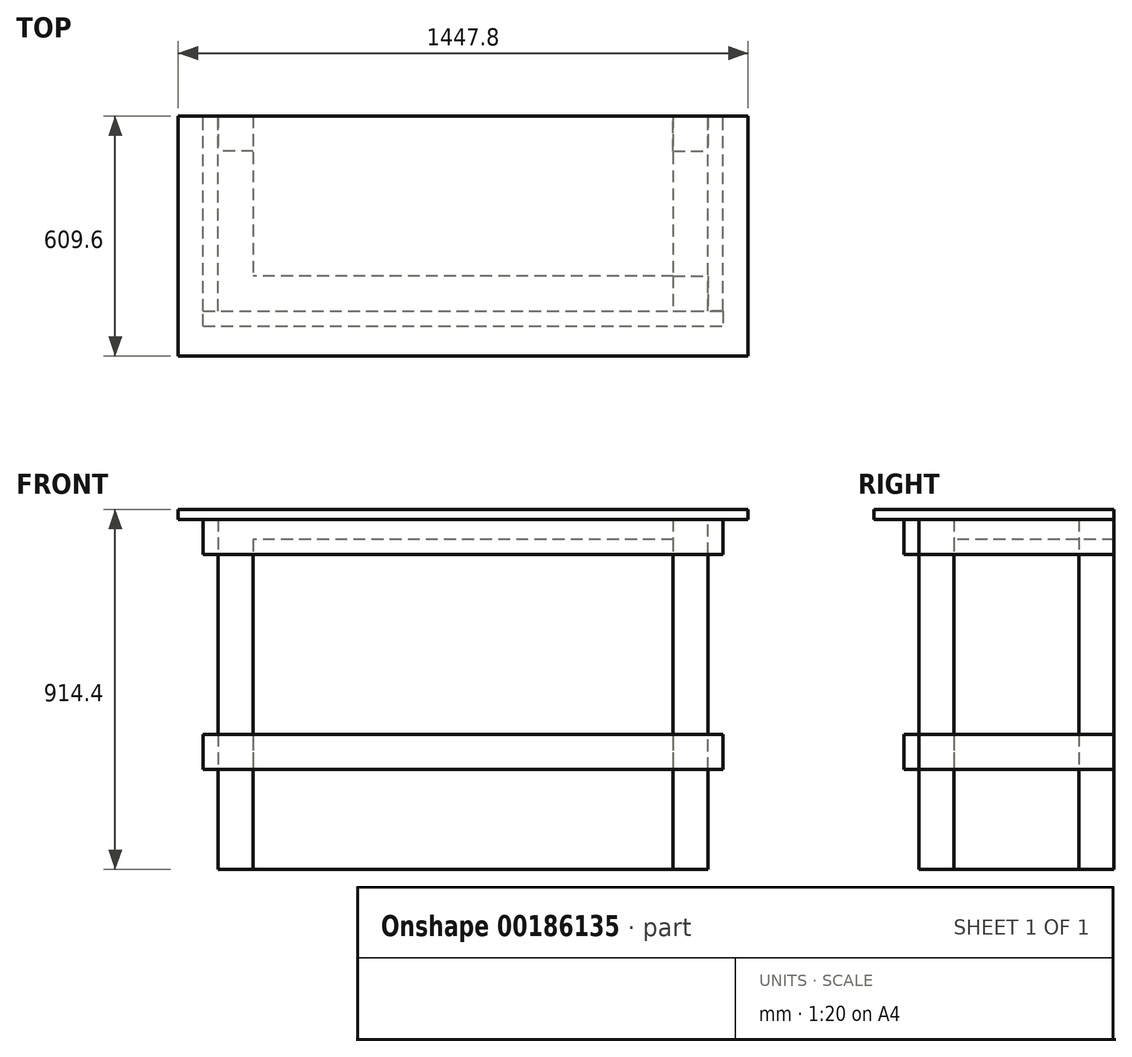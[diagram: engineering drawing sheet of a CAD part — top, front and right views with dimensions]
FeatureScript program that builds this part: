
annotation { "Feature Type Name" : "Feature", "Feature Type Description" : "" }
export const myFeature = defineFeature(function(context is Context, id is Id, definition is map)
    precondition{}
    {
        {
            var Q0;
            Q0=qCreatedBy(makeId("Top.planeOp"),FACE);
            var sketch = newSketch(context, id + "F0", { "sketchPlane" : qUnion([Q0])});
            skLineSegment(sketch, "E0.bottom", {"start": v(533.4, 203.2) * mm, "end": v(-533.4, 203.2) * mm});
            skLineSegment(sketch, "E0.top", {"start": v(533.4, -203.2) * mm, "end": v(-533.4, -203.2) * mm});
            skLineSegment(sketch, "E0.left", {"start": v(533.4, 203.2) * mm, "end": v(533.4, -203.2) * mm});
            skLineSegment(sketch, "E0.right", {"start": v(-533.4, 203.2) * mm, "end": v(-533.4, -203.2) * mm});
            skPoint(sketch, "E0.middle", {"position": v(0, 0) * mm});
            skSolve(sketch);
        }
        {
            var Q0;
            Q0=makeQuery(id+"F0.imprint","IMPRINT",FACE,{"disambiguationData":[TD([[makeQuery(id+"F0.imprint","IMPRINT",EDGE,{"derivedFrom":sQuery(id+"F0.wireOp",EDGE,"E0.bottom")}),1.0]])]});
            extrude(context, id + "F1", {"entities" : qUnion([Q0]), "depth" : 838.2 * mm});
        }
        {
            var Q0;
            Q0=qCreatedBy(makeId("Top.planeOp"),FACE);
            var sketch = newSketch(context, id + "F2", { "sketchPlane" : qUnion([Q0])});
            skLineSegment(sketch, "E1.bottom", {"start": v(-533.4, 203.2) * mm, "end": v(-622.3, 203.2) * mm});
            skLineSegment(sketch, "E1.top", {"start": v(-533.4, 114.3) * mm, "end": v(-622.3, 114.3) * mm});
            skLineSegment(sketch, "E1.left", {"start": v(-533.4, 203.2) * mm, "end": v(-533.4, 114.3) * mm});
            skLineSegment(sketch, "E1.right", {"start": v(-622.3, 203.2) * mm, "end": v(-622.3, 114.3) * mm});
            skPoint(sketch, "E1.middle", {"position": v(-577.85, 158.75) * mm});
            skLineSegment(sketch, "E2.0", {"start": v(533.4, 203.2) * mm, "end": v(-533.4, 203.2) * mm});
            skLineSegment(sketch, "E3", {"start": v(-533.4, 203.2) * mm, "end": v(-674.08, 203.2) * mm, "construction": true});
            skLineSegment(sketch, "E4.0.0", {"start": v(533.4, -203.2) * mm, "end": v(533.4, 203.2) * mm});
            skLineSegment(sketch, "E4.0.2", {"start": v(-533.4, 203.2) * mm, "end": v(-533.4, -203.2) * mm});
            skLineSegment(sketch, "E4.0.3", {"start": v(-533.4, -203.2) * mm, "end": v(533.4, -203.2) * mm});
            skLineSegment(sketch, "E5", {"start": v(-533.4, -203.2) * mm, "end": v(-657.88, -203.2) * mm});
            skLineSegment(sketch, "E6", {"start": v(-533.4, -203.2) * mm, "end": v(-533.4, -305.63) * mm});
            skLineSegment(sketch, "E7.bottom", {"start": v(-533.4, -203.2) * mm, "end": v(-622.3, -203.2) * mm});
            skLineSegment(sketch, "E7.top", {"start": v(-533.4, -292.1) * mm, "end": v(-622.3, -292.1) * mm});
            skLineSegment(sketch, "E7.left", {"start": v(-533.4, -203.2) * mm, "end": v(-533.4, -292.1) * mm});
            skLineSegment(sketch, "E7.right", {"start": v(-622.3, -203.2) * mm, "end": v(-622.3, -292.1) * mm});
            skPoint(sketch, "E7.middle", {"position": v(-577.85, -247.65) * mm});
            skLineSegment(sketch, "E8", {"start": v(0, 203.2) * mm, "end": v(0, -276.87) * mm});
            skLineSegment(sketch, "E9.MirrorCS", {"start": v(622.3, -203.2) * mm, "end": v(622.3, -292.1) * mm});
            skLineSegment(sketch, "E10.MirrorCS", {"start": v(533.4, -203.2) * mm, "end": v(533.4, -292.1) * mm});
            skLineSegment(sketch, "E11.MirrorCS", {"start": v(533.4, -203.2) * mm, "end": v(622.3, -203.2) * mm});
            skLineSegment(sketch, "E12.MirrorCS", {"start": v(533.4, -292.1) * mm, "end": v(622.3, -292.1) * mm});
            skPoint(sketch, "E13.MirrorP", {"position": v(577.85, -247.65) * mm});
            skLineSegment(sketch, "E14.MirrorCS", {"start": v(533.4, -203.2) * mm, "end": v(533.4, -305.63) * mm});
            skLineSegment(sketch, "E15.MirrorCS", {"start": v(533.4, 203.2) * mm, "end": v(622.3, 203.2) * mm});
            skLineSegment(sketch, "E16.MirrorCS", {"start": v(533.4, 203.2) * mm, "end": v(674.08, 203.2) * mm, "construction": true});
            skLineSegment(sketch, "E17.MirrorCS", {"start": v(622.3, 203.2) * mm, "end": v(622.3, 114.3) * mm});
            skLineSegment(sketch, "E18.MirrorCS", {"start": v(533.4, 203.2) * mm, "end": v(533.4, 114.3) * mm});
            skLineSegment(sketch, "E19.MirrorCS", {"start": v(533.4, 114.3) * mm, "end": v(622.3, 114.3) * mm});
            skPoint(sketch, "E20.MirrorP", {"position": v(577.85, 158.75) * mm});
            skSolve(sketch);
        }
        {
            var Q0;
            Q0=makeQuery(id+"F2.imprint","IMPRINT",FACE,{"disambiguationData":[TD([[makeQuery(id+"F2.imprint","IMPRINT",EDGE,{"derivedFrom":sQuery(id+"F2.wireOp",EDGE,"E1.bottom")}),1.0]])]});
            var Q1;
            Q1=makeQuery(id+"F2.imprint","IMPRINT",FACE,{"disambiguationData":[TD([[makeQuery(id+"F2.imprint","IMPRINT",EDGE,{"derivedFrom":sQuery(id+"F2.wireOp",EDGE,"E7.bottom")}),1.0]])]});
            var Q2;
            Q2=makeQuery(id+"F2.imprint","IMPRINT",FACE,{"disambiguationData":[TD([[makeQuery(id+"F2.imprint","IMPRINT",EDGE,{"derivedFrom":sQuery(id+"F2.wireOp",EDGE,"E12.MirrorCS")}),1.0]])]});
            var Q3;
            Q3=makeQuery(id+"F2.imprint","IMPRINT",FACE,{"disambiguationData":[TD([[makeQuery(id+"F2.imprint","IMPRINT",EDGE,{"derivedFrom":sQuery(id+"F2.wireOp",EDGE,"E15.MirrorCS")}),-1.0]])]});
            extrude(context, id + "F3", {"entities" : qUnion([Q0, Q1, Q2, Q3]), "depth" : 889 * mm});
        }
        {
            var Q0;
            Q0=makeQuery(id+"F1.opExtrude","SWEPT_FACE",FACE,{"disambiguationData":[OSD([sQuery(id+"F0.wireOp",EDGE,"E0.bottom")])]});
            var sketch = newSketch(context, id + "F4", { "sketchPlane" : qUnion([Q0])});
            skLineSegment(sketch, "E21", {"start": v(0, 0) * mm, "end": v(0, 390.8) * mm});
            skPoint(sketch, "E21.endSnap0", {"position": v(0, 0) * mm});
            skLineSegment(sketch, "E22.bottom", {"start": v(-622.3, 342.9) * mm, "end": v(-660.4, 342.9) * mm});
            skLineSegment(sketch, "E22.top", {"start": v(-622.3, 254) * mm, "end": v(-660.4, 254) * mm});
            skLineSegment(sketch, "E22.left", {"start": v(-622.3, 342.9) * mm, "end": v(-622.3, 254) * mm});
            skLineSegment(sketch, "E22.right", {"start": v(-660.4, 342.9) * mm, "end": v(-660.4, 254) * mm});
            skPoint(sketch, "E22.middle", {"position": v(-641.35, 298.45) * mm});
            skLineSegment(sketch, "E23.bottom", {"start": v(-622.3, 889) * mm, "end": v(-660.4, 889) * mm});
            skLineSegment(sketch, "E23.top", {"start": v(-622.3, 800.1) * mm, "end": v(-660.4, 800.1) * mm});
            skLineSegment(sketch, "E23.left", {"start": v(-622.3, 889) * mm, "end": v(-622.3, 800.1) * mm});
            skLineSegment(sketch, "E23.right", {"start": v(-660.4, 889) * mm, "end": v(-660.4, 800.1) * mm});
            skPoint(sketch, "E23.middle", {"position": v(-641.35, 844.55) * mm});
            skLineSegment(sketch, "E24.MirrorCS", {"start": v(622.3, 342.9) * mm, "end": v(660.4, 342.9) * mm});
            skLineSegment(sketch, "E25.MirrorCS", {"start": v(622.3, 342.9) * mm, "end": v(622.3, 254) * mm});
            skPoint(sketch, "E26.MirrorP", {"position": v(641.35, 844.55) * mm});
            skPoint(sketch, "E27.MirrorP", {"position": v(641.35, 298.45) * mm});
            skLineSegment(sketch, "E28.MirrorCS", {"start": v(622.3, 889) * mm, "end": v(660.4, 889) * mm});
            skLineSegment(sketch, "E29.MirrorCS", {"start": v(622.3, 254) * mm, "end": v(660.4, 254) * mm});
            skLineSegment(sketch, "E30.MirrorCS", {"start": v(660.4, 889) * mm, "end": v(660.4, 800.1) * mm});
            skLineSegment(sketch, "E31.MirrorCS", {"start": v(622.3, 889) * mm, "end": v(622.3, 800.1) * mm});
            skLineSegment(sketch, "E32.MirrorCS", {"start": v(660.4, 342.9) * mm, "end": v(660.4, 254) * mm});
            skLineSegment(sketch, "E33.MirrorCS", {"start": v(622.3, 800.1) * mm, "end": v(660.4, 800.1) * mm});
            skSolve(sketch);
        }
        {
            var Q0;
            Q0=makeQuery(id+"F4.imprint","IMPRINT",FACE,{"disambiguationData":[TD([[makeQuery(id+"F4.imprint","IMPRINT",EDGE,{"derivedFrom":sQuery(id+"F4.wireOp",EDGE,"E23.bottom")}),1.0]])]});
            var Q1;
            Q1=makeQuery(id+"F4.imprint","IMPRINT",FACE,{"disambiguationData":[TD([[makeQuery(id+"F4.imprint","IMPRINT",EDGE,{"derivedFrom":sQuery(id+"F4.wireOp",EDGE,"E22.bottom")}),1.0]])]});
            var Q2;
            Q2=makeQuery(id+"F4.imprint","IMPRINT",FACE,{"disambiguationData":[TD([[makeQuery(id+"F4.imprint","IMPRINT",EDGE,{"derivedFrom":sQuery(id+"F4.wireOp",EDGE,"E24.MirrorCS")}),-1.0]])]});
            var Q3;
            Q3=makeQuery(id+"F4.imprint","IMPRINT",FACE,{"disambiguationData":[TD([[makeQuery(id+"F4.imprint","IMPRINT",EDGE,{"derivedFrom":sQuery(id+"F4.wireOp",EDGE,"E28.MirrorCS")}),-1.0]])]});
            var Q4;
            Q4=makeQuery(id+"F3.opExtrude","SWEPT_FACE",FACE,{"disambiguationData":[OSD([sQuery(id+"F2.wireOp",EDGE,"E12.MirrorCS")])]});
            extrude(context, id + "F5", {"entities" : qUnion([Q0, Q1, Q2, Q3]), "endBound" : BoundingType.UP_TO_SURFACE, "oppositeDirection" : true, "endBoundEntityFace" : qUnion([Q4]), "depth" : 25.4 * mm});
        }
        {
            var Q0;
            Q0=makeQuery(id+"F5.opExtrude","SWEPT_FACE",FACE,{"disambiguationData":[OSD([sQuery(id+"F4.wireOp",EDGE,"E23.right")])]});
            var sketch = newSketch(context, id + "F6", { "sketchPlane" : qUnion([Q0])});
            skLineSegment(sketch, "E34.bottom", {"start": v(-292.1, 889) * mm, "end": v(-330.2, 889) * mm});
            skLineSegment(sketch, "E34.top", {"start": v(-292.1, 800.1) * mm, "end": v(-330.2, 800.1) * mm});
            skLineSegment(sketch, "E34.left", {"start": v(-292.1, 889) * mm, "end": v(-292.1, 800.1) * mm});
            skLineSegment(sketch, "E34.right", {"start": v(-330.2, 889) * mm, "end": v(-330.2, 800.1) * mm});
            skPoint(sketch, "E34.middle", {"position": v(-311.15, 844.55) * mm});
            skLineSegment(sketch, "E35.bottom", {"start": v(-292.1, 342.9) * mm, "end": v(-330.2, 342.9) * mm});
            skLineSegment(sketch, "E35.top", {"start": v(-292.1, 254) * mm, "end": v(-330.2, 254) * mm});
            skLineSegment(sketch, "E35.left", {"start": v(-292.1, 342.9) * mm, "end": v(-292.1, 254) * mm});
            skLineSegment(sketch, "E35.right", {"start": v(-330.2, 342.9) * mm, "end": v(-330.2, 254) * mm});
            skPoint(sketch, "E35.middle", {"position": v(-311.15, 298.45) * mm});
            skSolve(sketch);
        }
        {
            var Q0;
            Q0=makeQuery(id+"F6.imprint","IMPRINT",FACE,{"disambiguationData":[TD([[makeQuery(id+"F6.imprint","IMPRINT",EDGE,{"derivedFrom":sQuery(id+"F6.wireOp",EDGE,"E34.bottom")}),1.0]])]});
            var Q1;
            Q1=makeQuery(id+"F6.imprint","IMPRINT",FACE,{"disambiguationData":[TD([[makeQuery(id+"F6.imprint","IMPRINT",EDGE,{"derivedFrom":sQuery(id+"F6.wireOp",EDGE,"E35.bottom")}),1.0]])]});
            var Q2;
            Q2=makeQuery(id+"F5.opExtrude","SWEPT_FACE",FACE,{"disambiguationData":[OSD([sQuery(id+"F4.wireOp",EDGE,"E30.MirrorCS")])]});
            extrude(context, id + "F7", {"entities" : qUnion([Q0, Q1]), "endBound" : BoundingType.UP_TO_SURFACE, "oppositeDirection" : true, "endBoundEntityFace" : qUnion([Q2]), "depth" : 25.4 * mm});
        }
        {
            var Q0;
            Q0=makeQuery(id+"F3.opExtrude","CAP_FACE",FACE,{"disambiguationData":[OSD([sQuery(id+"F2.wireOp",EDGE,"E1.bottom"),sQuery(id+"F2.wireOp",EDGE,"E1.top"),sQuery(id+"F2.wireOp",EDGE,"E1.left"),sQuery(id+"F2.wireOp",EDGE,"E1.right")])],"isStart":false});
            var sketch = newSketch(context, id + "F8", { "sketchPlane" : qUnion([Q0])});
            skLineSegment(sketch, "E36.bottom", {"start": v(-723.9, 203.2) * mm, "end": v(723.9, 203.2) * mm});
            skLineSegment(sketch, "E36.top", {"start": v(-723.9, -406.4) * mm, "end": v(723.9, -406.4) * mm});
            skLineSegment(sketch, "E36.left", {"start": v(-723.9, 203.2) * mm, "end": v(-723.9, -406.4) * mm});
            skLineSegment(sketch, "E36.right", {"start": v(723.9, 203.2) * mm, "end": v(723.9, -406.4) * mm});
            skSolve(sketch);
        }
        {
            var Q0;
            Q0=makeQuery(id+"F8.imprint","IMPRINT",FACE,{"disambiguationData":[TD([[makeQuery(id+"F8.imprint","IMPRINT",EDGE,{"derivedFrom":sQuery(id+"F8.wireOp",EDGE,"E36.top")}),1.0]])]});
            var Q1;
            Q1=makeQuery(id+"F8.imprint","IMPRINT",FACE,{"disambiguationData":[TD([[makeQuery(id+"F8.imprint","IMPRINT",EDGE,{"derivedFrom":makeQuery(id+"F3.opExtrude","CAP_EDGE",EDGE,{"disambiguationData":[OSD([sQuery(id+"F2.wireOp",EDGE,"E1.top")])],"isStart":false})}),-1.0]])]});
            extrude(context, id + "F9", {"entities" : qUnion([Q0, Q1]), "depth" : 25.4 * mm});
        }
    });
